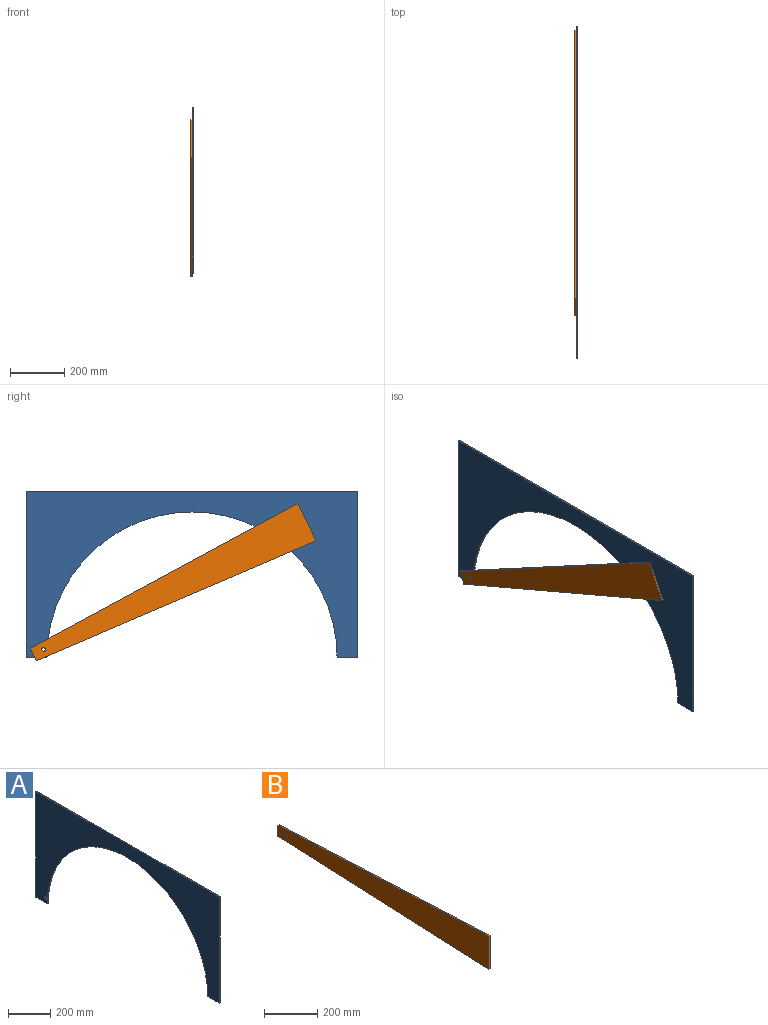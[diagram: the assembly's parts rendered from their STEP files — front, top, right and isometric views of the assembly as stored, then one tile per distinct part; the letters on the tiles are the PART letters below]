
ASSEMBLY  parts=2 mates=1
PART A: 9 faces, bbox 6.4x1219.2x609.6 mm
  f0: cylinder r=533.4mm len=1066.8mm, axis (-1,0,0), area 10640.9mm2, adj f1,f6,f7,f8
  f1: plane 76.2x6.35mm, normal (0,0,-1), area 483.9mm2, adj f0,f2,f7,f8
  f2: plane 609.6x6.35mm, normal (0,1,0), area 3871mm2, adj f1,f3,f7,f8
  f3: plane 1219.2x6.35mm, normal (0,0,1), area 7741.9mm2, adj f2,f4,f7,f8
  f4: plane 609.6x6.35mm, normal (0,-1,0), area 3871mm2, adj f3,f6,f7,f8
  f5: cylinder r=6.35mm len=12.7mm, axis (-1,0,0), area 253.4mm2, adj f7,f8
  f6: plane 76.2x6.35mm, normal (0,0,-1), area 483.9mm2, adj f0,f4,f7,f8
  f7: plane 1219.2x609.6mm, normal (1,0,0), area 296181.6mm2, adj f0,f1,f2,f3,f4,f5,f6
  f8: plane 1219.2x609.6mm, normal (-1,0,0), area 296181.6mm2, adj f0,f1,f2,f3,f4,f5,f6
PART B: 7 faces, bbox 6.4x1117.6x152.4 mm
  f0: plane 1117.6x50.8mm, normal (0,0.05,1), area 7104.1mm2, adj f1,f4,f5,f6
  f1: plane 152.4x6.35mm, normal (0,-1,0), area 967.7mm2, adj f0,f2,f5,f6
  f2: plane 1117.6x50.8mm, normal (0,0.05,-1), area 7104.1mm2, adj f1,f4,f5,f6
  f3: cylinder r=6.35mm len=12.7mm, axis (-1,0,0), area 253.4mm2, adj f5,f6
  f4: plane 50.8x6.35mm, normal (0,1,0), area 322.6mm2, adj f0,f2,f5,f6
  f5: plane 1117.6x152.4mm, normal (1,0,0), area 113421.5mm2, adj f0,f1,f2,f3,f4
  f6: plane 1117.6x152.4mm, normal (-1,0,0), area 113421.5mm2, adj f0,f1,f2,f3,f4
PLACE A t=(-3.17,-211.58,158.64)mm fixed
PLACE B rot(axis=(-1,0,0),25.8deg) t=(-9.52,-130.69,106.22)mm
MATE revolute B.f3 <-> A.f5  axis (1,0,0) through (-3.17,333.69,-118.07)mm
